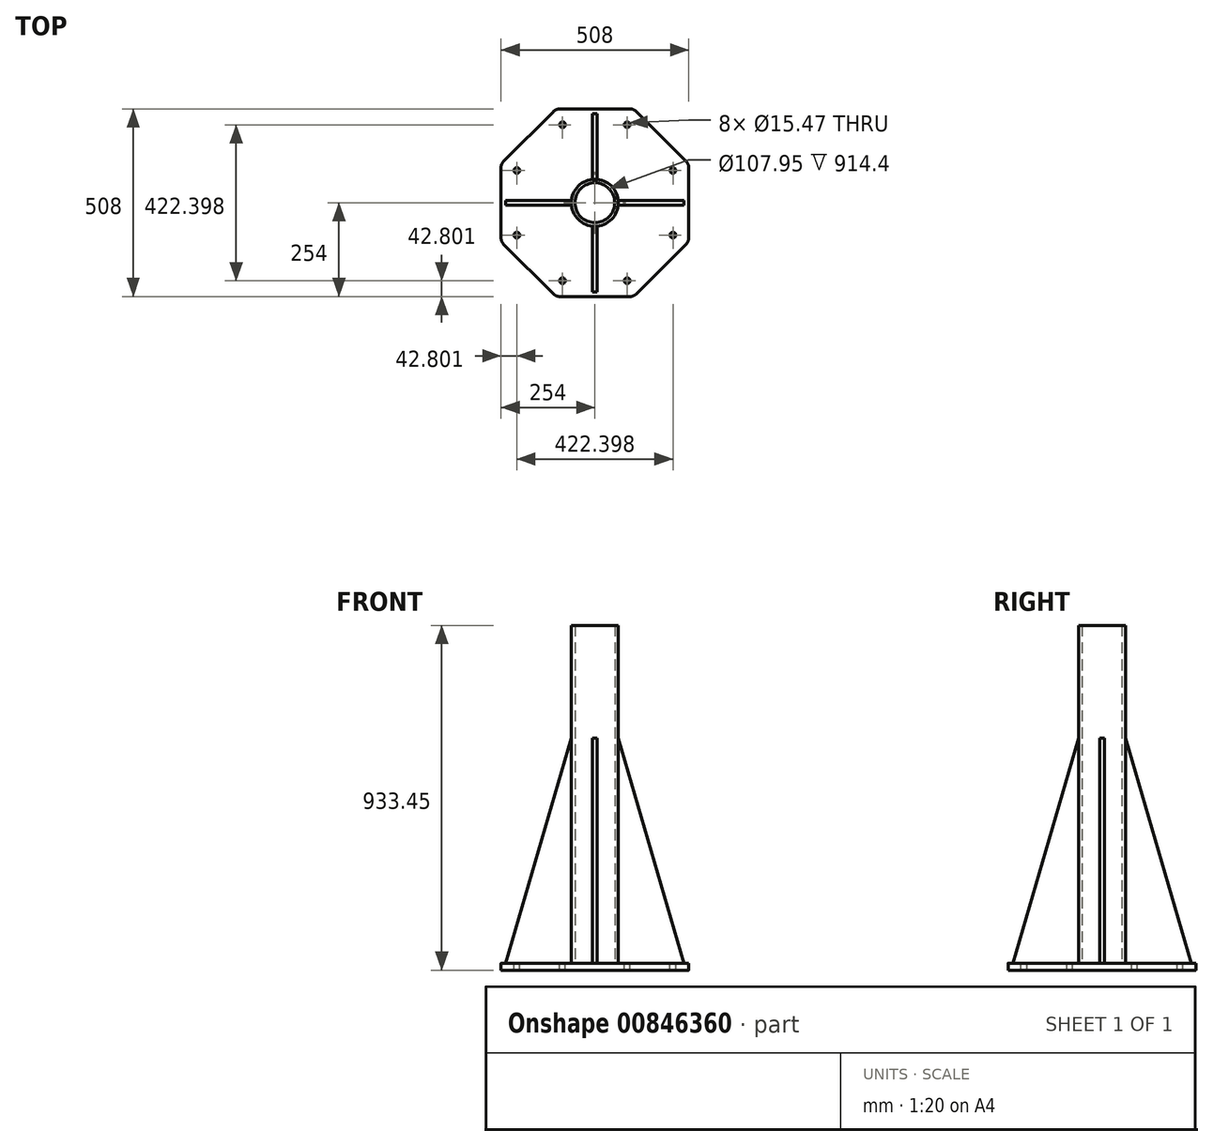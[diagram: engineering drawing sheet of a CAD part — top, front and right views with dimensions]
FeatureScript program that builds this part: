
annotation { "Feature Type Name" : "Feature", "Feature Type Description" : "" }
export const myFeature = defineFeature(function(context is Context, id is Id, definition is map)
    precondition{}
    {
        {
            var Q0;
            Q0=qCreatedBy(makeId("Top.planeOp"),FACE);
            var sketch = newSketch(context, id + "F0", { "sketchPlane" : qUnion([Q0])});
            skCircle(sketch, "E0.cCircle", {"center": v(0, 0) * mm, "radius": 254 * mm, "construction": true});
            skLineSegment(sketch, "E0.0", {"start": v(-105.21, 254) * mm, "end": v(105.21, 254) * mm});
            skLineSegment(sketch, "E0.1", {"start": v(105.21, 254) * mm, "end": v(254, 105.21) * mm});
            skLineSegment(sketch, "E0.2", {"start": v(254, 105.21) * mm, "end": v(254, -105.21) * mm});
            skLineSegment(sketch, "E0.3", {"start": v(254, -105.21) * mm, "end": v(105.21, -254) * mm});
            skLineSegment(sketch, "E0.4", {"start": v(105.21, -254) * mm, "end": v(-105.21, -254) * mm});
            skLineSegment(sketch, "E0.5", {"start": v(-105.21, -254) * mm, "end": v(-254, -105.21) * mm});
            skLineSegment(sketch, "E0.6", {"start": v(-254, -105.21) * mm, "end": v(-254, 105.21) * mm});
            skLineSegment(sketch, "E0.7", {"start": v(-254, 105.21) * mm, "end": v(-105.21, 254) * mm});
            skPoint(sketch, "E0.0.midPoint", {"position": v(0, 254) * mm});
            skSolve(sketch);
        }
        {
            var Q0;
            Q0 = qSketchRegion(id + "F0", true);
            extrude(context, id + "F1", {"entities" : qUnion([Q0]), "depth" : 19.05 * mm, "offsetDistance" : 25.4 * mm});
        }
        {
            var Q0;
            Q0=makeQuery(id+"F1.opExtrude","CAP_FACE",FACE,{"disambiguationData":[OSD([sQuery(id+"F0.wireOp",EDGE,"E0.0"),sQuery(id+"F0.wireOp",EDGE,"E0.1"),sQuery(id+"F0.wireOp",EDGE,"E0.2"),sQuery(id+"F0.wireOp",EDGE,"E0.3"),sQuery(id+"F0.wireOp",EDGE,"E0.4"),sQuery(id+"F0.wireOp",EDGE,"E0.5"),sQuery(id+"F0.wireOp",EDGE,"E0.6"),sQuery(id+"F0.wireOp",EDGE,"E0.7")])],"isStart":false});
            var sketch = newSketch(context, id + "F2", { "sketchPlane" : qUnion([Q0])});
            skCircle(sketch, "E1", {"center": v(0, 0) * mm, "radius": 53.98 * mm});
            skCircle(sketch, "E2.0", {"center": v(0, 0) * mm, "radius": 63.5 * mm});
            skSolve(sketch);
        }
        {
            var Q0;
            Q0 = qSketchRegion(id + "F2", true);
            extrude(context, id + "F3", {"entities" : qUnion([Q0]), "operationType" : NewBodyOperationType.ADD, "depth" : 914.4 * mm, "offsetDistance" : 25.4 * mm});
        }
        {
            var Q0;
            Q0=qCreatedBy(makeId("Front.planeOp"),FACE);
            var sketch = newSketch(context, id + "F4", { "sketchPlane" : qUnion([Q0])});
            skLineSegment(sketch, "E3", {"start": v(63.5, 628.65) * mm, "end": v(241.3, 19.05) * mm});
            skLineSegment(sketch, "E4", {"start": v(241.3, 19.05) * mm, "end": v(63.5, 19.05) * mm});
            skPoint(sketch, "E5.endSnap0", {"position": v(152.4, 19.05) * mm});
            skLineSegment(sketch, "E6", {"start": v(63.5, 628.65) * mm, "end": v(63.5, 19.05) * mm});
            skSolve(sketch);
        }
        {
            var Q0;
            Q0 = qSketchRegion(id + "F4", true);
            extrude(context, id + "F5", {"entities" : qUnion([Q0]), "endBound" : BoundingType.SYMMETRIC, "depth" : 12.7 * mm, "offsetDistance" : 25.4 * mm});
        }
        {
            var Q0;
            Q0=makeQuery(id+"F5.opExtrude","SWEPT_BODY",BODY,{"disambiguationData":[OSD([sQuery(id+"F4.wireOp",EDGE,"E3"),sQuery(id+"F4.wireOp",EDGE,"E4"),sQuery(id+"F4.wireOp",EDGE,"E6")])]});
            var Q1;
            Q1=makeQuery(id+"F3.opExtrude","SWEPT_FACE",FACE,{"disambiguationData":[OSD([sQuery(id+"F2.wireOp",EDGE,"E2.0")])]});
            circularPattern(context, id + "F6", {"entities" : qUnion([Q0]), "axis" : qUnion([Q1]), "angle" : 360 * degree, "instanceCount" : 4, "equalSpace" : true});
        }
        {
            var Q0;
            {var subQ0=sQuery(id+"F0.wireOp",EDGE,"E0.2");var subQ1=sQuery(id+"F0.wireOp",EDGE,"E0.1");var subQ2=sQuery(id+"F0.wireOp",EDGE,"E0.3");var subQ3=sQuery(id+"F0.wireOp",EDGE,"E0.0");var subQ4=sQuery(id+"F0.wireOp",EDGE,"E0.4");var subQ5=sQuery(id+"F0.wireOp",EDGE,"E0.5");var subQ6=sQuery(id+"F0.wireOp",EDGE,"E0.6");var subQ7=sQuery(id+"F0.wireOp",EDGE,"E0.7");Q0=makeQuery(id+"F3.boolean.opBoolean","SPLIT",FACE,{"disambiguationData":[TD([makeQuery(id+"F1.opExtrude","SWEPT_FACE",FACE,{"disambiguationData":[OSD([subQ3])]})])],"derivedFrom":makeQuery(id+"F1.opExtrude","CAP_FACE",FACE,{"disambiguationData":[OSD([subQ3,subQ1,subQ0,subQ2,subQ4,subQ5,subQ6,subQ7])],"isStart":false})});}
            var sketch = newSketch(context, id + "F7", { "sketchPlane" : qUnion([Q0])});
            skPoint(sketch, "E7", {"position": v(211.2, -87.48) * mm});
            skLineSegment(sketch, "E8", {"start": v(0, 0) * mm, "end": v(211.2, -87.48) * mm});
            skLineSegment(sketch, "E9", {"start": v(211.2, -87.48) * mm, "end": v(254, -105.21) * mm});
            skCircle(sketch, "E10", {"center": v(0, 0) * mm, "radius": 228.6 * mm});
            skPoint(sketch, "E11.1.0", {"position": v(211.2, 87.48) * mm});
            skPoint(sketch, "E11.2.0", {"position": v(87.48, 211.2) * mm});
            skPoint(sketch, "E11.3.0", {"position": v(-87.48, 211.2) * mm});
            skPoint(sketch, "E11.4.0", {"position": v(-211.2, 87.48) * mm});
            skPoint(sketch, "E11.5.0", {"position": v(-211.2, -87.48) * mm});
            skPoint(sketch, "E11.6.0", {"position": v(-87.48, -211.2) * mm});
            skPoint(sketch, "E11.7.0", {"position": v(87.48, -211.2) * mm});
            skSolve(sketch);
        }
        {
            var Q0;
            Q0=sQuery(id+"F7.wireOp",VERTEX,"E11.7.0");
            var Q1;
            Q1=sQuery(id+"F7.wireOp",VERTEX,"E7");
            var Q2;
            Q2=sQuery(id+"F7.wireOp",VERTEX,"E11.1.0");
            var Q3;
            Q3=sQuery(id+"F7.wireOp",VERTEX,"E11.2.0");
            var Q4;
            Q4=sQuery(id+"F7.wireOp",VERTEX,"E11.3.0");
            var Q5;
            Q5=sQuery(id+"F7.wireOp",VERTEX,"E11.4.0");
            var Q6;
            Q6=sQuery(id+"F7.wireOp",VERTEX,"E11.5.0");
            var Q7;
            Q7=sQuery(id+"F7.wireOp",VERTEX,"E11.6.0");
            var Q8;
            Q8=makeQuery(id+"F1.opExtrude","SWEPT_BODY",BODY,{"disambiguationData":[OSD([sQuery(id+"F0.wireOp",EDGE,"E0.0"),sQuery(id+"F0.wireOp",EDGE,"E0.1"),sQuery(id+"F0.wireOp",EDGE,"E0.2"),sQuery(id+"F0.wireOp",EDGE,"E0.3"),sQuery(id+"F0.wireOp",EDGE,"E0.4"),sQuery(id+"F0.wireOp",EDGE,"E0.5"),sQuery(id+"F0.wireOp",EDGE,"E0.6"),sQuery(id+"F0.wireOp",EDGE,"E0.7")])]});
            hole(context, id + "F8", {"style" : HoleStyle.SIMPLE, "endStyle" : HoleEndStyle.THROUGH, "standardTappedOrClearance" : lookupTablePath({ "fit" : "Loose (ASME)", "standard" : "ANSI", "size" : "1/2", "type" : "Clearance" }), "standardBlindInLast" : lookupTablePath({ "fit" : "Loose", "standard" : "ANSI", "size" : "1/2", "type" : "Clearance" }), "holeDiameter" : 15.47 * mm, "majorDiameter" : 6.35 * mm, "isTappedThrough" : true, "tappedDepth" : 12.7 * mm, "tapClearance" : 3, "locations" : qUnion([Q0, Q1, Q2, Q3, Q4, Q5, Q6, Q7]), "scope" : qUnion([Q8])});
        }
        {
            var Q0;
            Q0=makeQuery(id+"F1.opExtrude","SWEPT_EDGE",EDGE,{"disambiguationData":[OSD([sQuery(id+"F0.wireOp",EDGE,"E0.3"),sQuery(id+"F0.wireOp",EDGE,"E0.4")])]});
            var Q1;
            Q1=makeQuery(id+"F1.opExtrude","SWEPT_EDGE",EDGE,{"disambiguationData":[OSD([sQuery(id+"F0.wireOp",EDGE,"E0.2"),sQuery(id+"F0.wireOp",EDGE,"E0.3")])]});
            var Q2;
            Q2=makeQuery(id+"F1.opExtrude","SWEPT_EDGE",EDGE,{"disambiguationData":[OSD([sQuery(id+"F0.wireOp",EDGE,"E0.1"),sQuery(id+"F0.wireOp",EDGE,"E0.2")])]});
            var Q3;
            Q3=makeQuery(id+"F1.opExtrude","SWEPT_EDGE",EDGE,{"disambiguationData":[OSD([sQuery(id+"F0.wireOp",EDGE,"E0.0"),sQuery(id+"F0.wireOp",EDGE,"E0.1")])]});
            var Q4;
            Q4=makeQuery(id+"F1.opExtrude","SWEPT_EDGE",EDGE,{"disambiguationData":[OSD([sQuery(id+"F0.wireOp",EDGE,"E0.0"),sQuery(id+"F0.wireOp",EDGE,"E0.7")])]});
            var Q5;
            Q5=makeQuery(id+"F1.opExtrude","SWEPT_EDGE",EDGE,{"disambiguationData":[OSD([sQuery(id+"F0.wireOp",EDGE,"E0.6"),sQuery(id+"F0.wireOp",EDGE,"E0.7")])]});
            var Q6;
            Q6=makeQuery(id+"F1.opExtrude","SWEPT_EDGE",EDGE,{"disambiguationData":[OSD([sQuery(id+"F0.wireOp",EDGE,"E0.5"),sQuery(id+"F0.wireOp",EDGE,"E0.6")])]});
            var Q7;
            Q7=makeQuery(id+"F1.opExtrude","SWEPT_EDGE",EDGE,{"disambiguationData":[OSD([sQuery(id+"F0.wireOp",EDGE,"E0.4"),sQuery(id+"F0.wireOp",EDGE,"E0.5")])]});
            fillet(context, id + "F9", {"entities" : qUnion([Q0, Q1, Q2, Q3, Q4, Q5, Q6, Q7]), "radius" : 25.4 * mm, "tangentPropagation" : true, "allowEdgeOverflow" : false});
        }
    });
